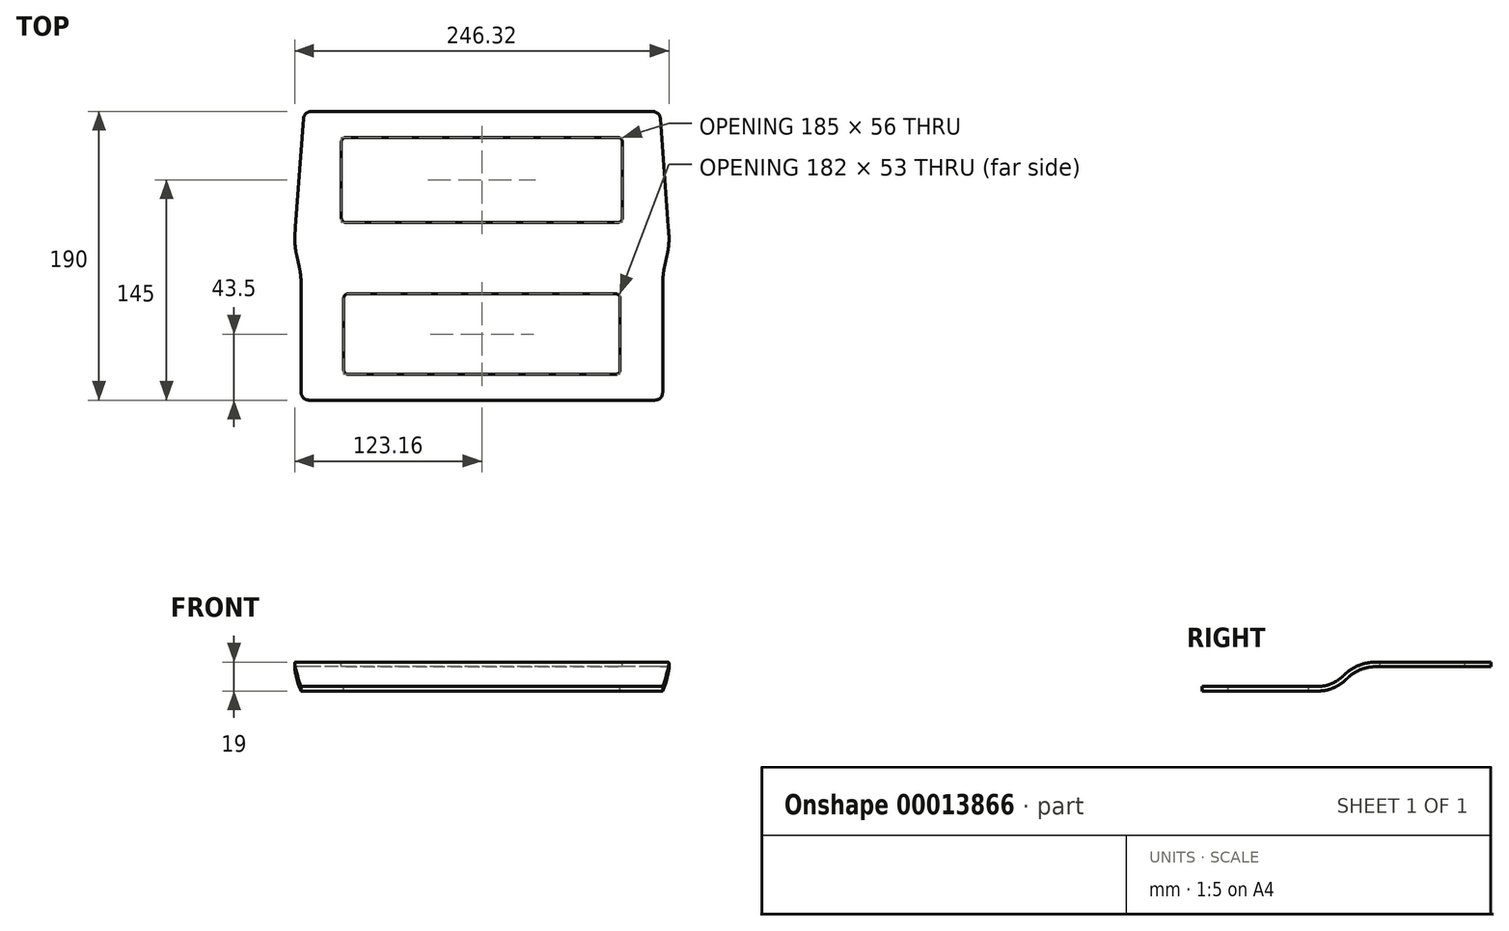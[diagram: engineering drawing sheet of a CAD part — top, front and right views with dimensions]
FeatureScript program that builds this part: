
annotation { "Feature Type Name" : "Feature", "Feature Type Description" : "" }
export const myFeature = defineFeature(function(context is Context, id is Id, definition is map)
    precondition{}
    {
        {
            var Q0;
            Q0=qCreatedBy(makeId("Right.planeOp"),FACE);
            var sketch = newSketch(context, id + "F0", { "sketchPlane" : qUnion([Q0])});
            skArc(sketch, "E0", {"start": v(19, 8) * mm, "mid": v(8.7, 5.92) * mm, "end": v(0, 0) * mm});
            skArc(sketch, "E1", {"start": v(-19, -8) * mm, "mid": v(-8.7, -5.92) * mm, "end": v(0, 0) * mm});
            skLineSegment(sketch, "E2", {"start": v(-19, -8) * mm, "end": v(-95, -8) * mm});
            skLineSegment(sketch, "E3", {"start": v(19, 8) * mm, "end": v(95, 8) * mm});
            skLineSegment(sketch, "E4", {"start": v(-19, -8) * mm, "end": v(-19, 0) * mm, "construction": true});
            skLineSegment(sketch, "E5", {"start": v(19, 8) * mm, "end": v(19, 0) * mm, "construction": true});
            skLineSegment(sketch, "E6", {"start": v(-19, 0) * mm, "end": v(0, 0) * mm, "construction": true});
            skLineSegment(sketch, "E7", {"start": v(19, 0) * mm, "end": v(0, 0) * mm, "construction": true});
            skLineSegment(sketch, "E8.0", {"start": v(19, 11) * mm, "end": v(95, 11) * mm});
            skArc(sketch, "E8.1", {"start": v(19, 11) * mm, "mid": v(7.53, 8.68) * mm, "end": v(-2.15, 2.1) * mm});
            skArc(sketch, "E8.2", {"start": v(-19, -5) * mm, "mid": v(-9.86, -3.15) * mm, "end": v(-2.15, 2.1) * mm});
            skLineSegment(sketch, "E8.3", {"start": v(-19, -5) * mm, "end": v(-95, -5) * mm});
            skLineSegment(sketch, "E9", {"start": v(95, 11) * mm, "end": v(95, 8) * mm});
            skLineSegment(sketch, "E10", {"start": v(-95, -5) * mm, "end": v(-95, -8) * mm});
            skSolve(sketch);
        }
        {
            var Q0;
            Q0 = qSketchRegion(id + "F0", true);
            extrude(context, id + "F1", {"entities" : qUnion([Q0]), "endBound" : BoundingType.SYMMETRIC, "depth" : 250 * mm});
        }
        {
            var Q0;
            Q0=makeQuery(id+"F1.opExtrude","SWEPT_FACE",FACE,{"disambiguationData":[OSD([sQuery(id+"F0.wireOp",EDGE,"E8.0")])]});
            var sketch = newSketch(context, id + "F2", { "sketchPlane" : qUnion([Q0])});
            skLineSegment(sketch, "E11.rect.bottom", {"start": v(-89.5, 78) * mm, "end": v(89.5, 78) * mm});
            skLineSegment(sketch, "E11.rect.top", {"start": v(-89.5, 22) * mm, "end": v(89.5, 22) * mm});
            skLineSegment(sketch, "E11.rect.left", {"start": v(-92.5, 75) * mm, "end": v(-92.5, 25) * mm});
            skLineSegment(sketch, "E11.rect.right", {"start": v(92.5, 75) * mm, "end": v(92.5, 25) * mm});
            skPoint(sketch, "E11.rect.middle", {"position": v(0, 50) * mm});
            skLineSegment(sketch, "E12.rect.bottom", {"start": v(-88, -25) * mm, "end": v(88, -25) * mm});
            skLineSegment(sketch, "E12.rect.top", {"start": v(-88, -78) * mm, "end": v(88, -78) * mm});
            skLineSegment(sketch, "E12.rect.left", {"start": v(-91, -28) * mm, "end": v(-91, -75) * mm});
            skLineSegment(sketch, "E12.rect.right", {"start": v(91, -28) * mm, "end": v(91, -75) * mm});
            skPoint(sketch, "E12.rect.middle", {"position": v(0, -51.5) * mm});
            skPoint(sketch, "E13.visualSharp", {"position": v(-92.5, 78) * mm});
            skArc(sketch, "E13.filletArc", {"start": v(-89.5, 78) * mm, "mid": v(-91.62, 77.12) * mm, "end": v(-92.5, 75) * mm});
            skPoint(sketch, "E14.visualSharp", {"position": v(92.5, 78) * mm});
            skArc(sketch, "E14.filletArc", {"start": v(92.5, 75) * mm, "mid": v(91.62, 77.12) * mm, "end": v(89.5, 78) * mm});
            skPoint(sketch, "E15.visualSharp", {"position": v(92.5, 22) * mm});
            skArc(sketch, "E15.filletArc", {"start": v(89.5, 22) * mm, "mid": v(91.62, 22.88) * mm, "end": v(92.5, 25) * mm});
            skPoint(sketch, "E16.visualSharp", {"position": v(-92.5, 22) * mm});
            skArc(sketch, "E16.filletArc", {"start": v(-92.5, 25) * mm, "mid": v(-91.62, 22.88) * mm, "end": v(-89.5, 22) * mm});
            skPoint(sketch, "E17.visualSharp", {"position": v(-91, -25) * mm});
            skArc(sketch, "E17.filletArc", {"start": v(-88, -25) * mm, "mid": v(-90.12, -25.88) * mm, "end": v(-91, -28) * mm});
            skPoint(sketch, "E18.visualSharp", {"position": v(-91, -78) * mm});
            skArc(sketch, "E18.filletArc", {"start": v(-91, -75) * mm, "mid": v(-90.12, -77.12) * mm, "end": v(-88, -78) * mm});
            skPoint(sketch, "E19.visualSharp", {"position": v(91, -25) * mm});
            skArc(sketch, "E19.filletArc", {"start": v(91, -28) * mm, "mid": v(90.12, -25.88) * mm, "end": v(88, -25) * mm});
            skPoint(sketch, "E20.visualSharp", {"position": v(91, -78) * mm});
            skArc(sketch, "E20.filletArc", {"start": v(88, -78) * mm, "mid": v(90.12, -77.12) * mm, "end": v(91, -75) * mm});
            skSolve(sketch);
        }
        {
            var Q0;
            Q0 = qSketchRegion(id + "F2", true);
            extrude(context, id + "F3", {"entities" : qUnion([Q0]), "operationType" : NewBodyOperationType.REMOVE, "endBound" : BoundingType.THROUGH_ALL, "oppositeDirection" : true, "depth" : 25 * mm});
        }
        {
            var Q0;
            Q0=makeQuery(id+"F2.imprint","IMPRINT",FACE,{"disambiguationData":[TD([[makeQuery(id+"F2.imprint","IMPRINT",EDGE,{"derivedFrom":sQuery(id+"F2.wireOp",EDGE,"E11.rect.bottom")}),1.0]])]});
            var sketch = newSketch(context, id + "F4", { "sketchPlane" : qUnion([Q0])});
            skLineSegment(sketch, "E21", {"start": v(0, 95) * mm, "end": v(-112.51, 95) * mm});
            skLineSegment(sketch, "E22", {"start": v(-117.5, 90.36) * mm, "end": v(-123.04, 14.61) * mm});
            skLineSegment(sketch, "E23", {"start": v(-122.11, 1.46) * mm, "end": v(-120.3, -6.82) * mm});
            skLineSegment(sketch, "E24", {"start": v(-119, -19) * mm, "end": v(-119, -90) * mm});
            skLineSegment(sketch, "E25", {"start": v(-114, -95) * mm, "end": v(0, -95) * mm});
            skPoint(sketch, "E26.visualSharp", {"position": v(-117.16, 95) * mm});
            skArc(sketch, "E26.filletArc", {"start": v(-112.51, 95) * mm, "mid": v(-115.92, 93.66) * mm, "end": v(-117.5, 90.36) * mm});
            skPoint(sketch, "E27.visualSharp", {"position": v(-123.53, 7.97) * mm});
            skArc(sketch, "E27.filletArc", {"start": v(-123.04, 14.61) * mm, "mid": v(-123.05, 8) * mm, "end": v(-122.11, 1.46) * mm});
            skPoint(sketch, "E28.visualSharp", {"position": v(-119, -12.84) * mm});
            skArc(sketch, "E28.filletArc", {"start": v(-119, -19) * mm, "mid": v(-119.33, -12.88) * mm, "end": v(-120.3, -6.82) * mm});
            skPoint(sketch, "E29.visualSharp", {"position": v(-117.5, -95) * mm});
            skArc(sketch, "E29.filletArc", {"start": v(-119, -90) * mm, "mid": v(-117.54, -93.54) * mm, "end": v(-114, -95) * mm});
            skLineSegment(sketch, "E30", {"start": v(0, 95) * mm, "end": v(0, -95) * mm, "construction": true});
            skLineSegment(sketch, "E31.MirrorCS", {"start": v(0, 95) * mm, "end": v(112.51, 95) * mm});
            skArc(sketch, "E32.MirrorCS", {"start": v(112.51, 95) * mm, "mid": v(115.92, 93.66) * mm, "end": v(117.5, 90.36) * mm});
            skLineSegment(sketch, "E33.MirrorCS", {"start": v(117.5, 90.36) * mm, "end": v(123.04, 14.61) * mm});
            skArc(sketch, "E34.MirrorCS", {"start": v(123.04, 14.61) * mm, "mid": v(123.05, 8) * mm, "end": v(122.11, 1.46) * mm});
            skLineSegment(sketch, "E35.MirrorCS", {"start": v(122.11, 1.46) * mm, "end": v(120.3, -6.82) * mm});
            skArc(sketch, "E36.MirrorCS", {"start": v(119, -19) * mm, "mid": v(119.33, -12.88) * mm, "end": v(120.3, -6.82) * mm});
            skLineSegment(sketch, "E37.MirrorCS", {"start": v(119, -19) * mm, "end": v(119, -90) * mm});
            skArc(sketch, "E38.MirrorCS", {"start": v(119, -90) * mm, "mid": v(117.54, -93.54) * mm, "end": v(114, -95) * mm});
            skLineSegment(sketch, "E39.MirrorCS", {"start": v(114, -95) * mm, "end": v(0, -95) * mm});
            skLineSegment(sketch, "E40", {"start": v(-122.5, 22) * mm, "end": v(122.5, 22) * mm, "construction": true});
            skLineSegment(sketch, "E41", {"start": v(-123.05, 8) * mm, "end": v(123.05, 8) * mm, "construction": true});
            skLineSegment(sketch, "E42", {"start": v(-125, -19) * mm, "end": v(-119, -19) * mm, "construction": true});
            skLineSegment(sketch, "E43.rect.bottom", {"start": v(166.5, -113.76) * mm, "end": v(-166.5, -113.76) * mm});
            skLineSegment(sketch, "E43.rect.top", {"start": v(166.5, 113.76) * mm, "end": v(-166.5, 113.76) * mm});
            skLineSegment(sketch, "E43.rect.left", {"start": v(166.5, -113.76) * mm, "end": v(166.5, 113.76) * mm});
            skLineSegment(sketch, "E43.rect.right", {"start": v(-166.5, -113.76) * mm, "end": v(-166.5, 113.76) * mm});
            skPoint(sketch, "E43.rect.middle", {"position": v(0, 0) * mm});
            skSolve(sketch);
        }
        {
            var Q0;
            Q0 = qSketchRegion(id + "F4", true);
            extrude(context, id + "F5", {"entities" : qUnion([Q0]), "operationType" : NewBodyOperationType.REMOVE, "endBound" : BoundingType.THROUGH_ALL, "oppositeDirection" : true, "depth" : 25 * mm});
        }
    });
